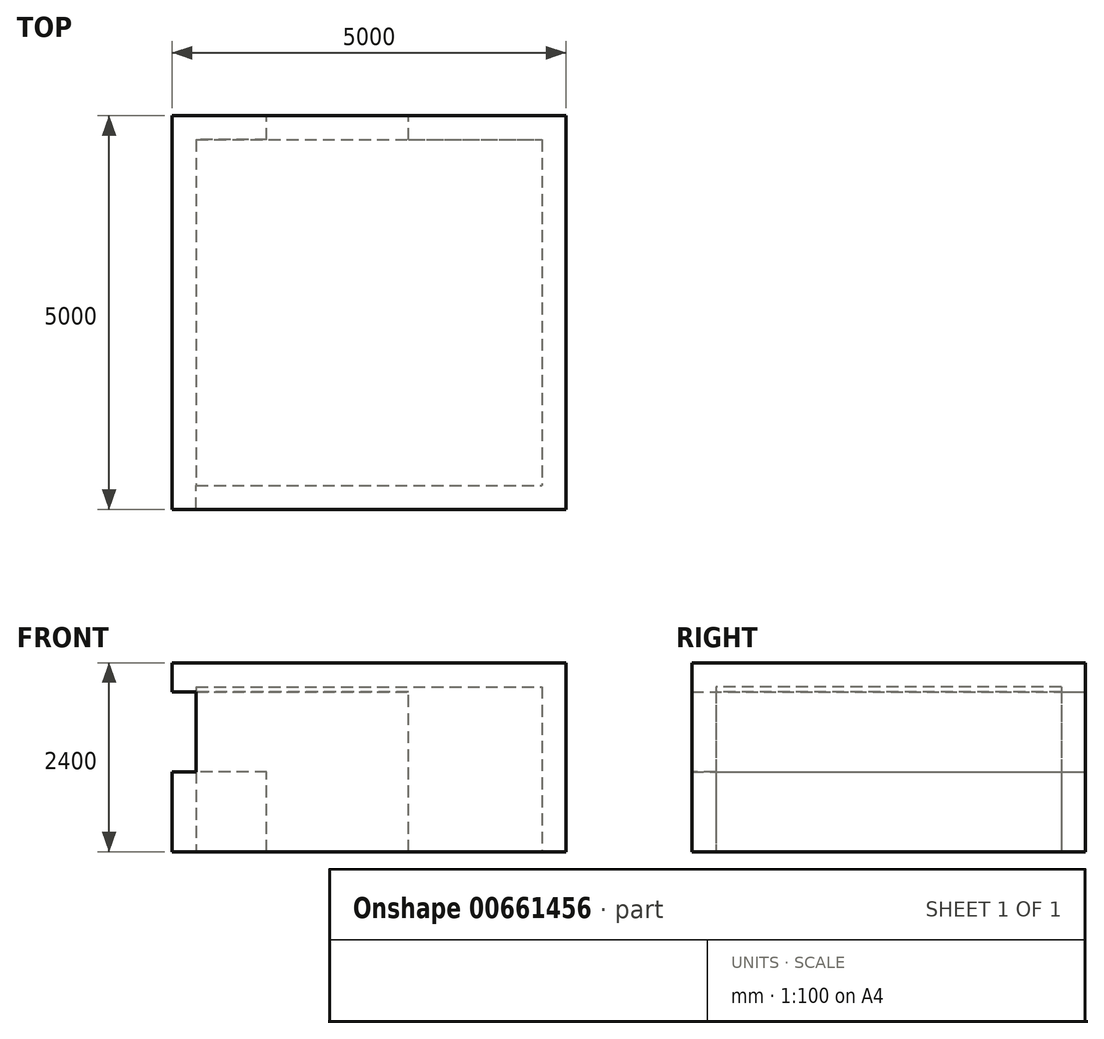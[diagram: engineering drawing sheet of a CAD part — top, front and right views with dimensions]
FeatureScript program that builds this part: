
annotation { "Feature Type Name" : "Feature", "Feature Type Description" : "" }
export const myFeature = defineFeature(function(context is Context, id is Id, definition is map)
    precondition{}
    {
        {
            var Q0;
            Q0=qCreatedBy(makeId("Top.planeOp"),FACE);
            var sketch = newSketch(context, id + "F0", { "sketchPlane" : qUnion([Q0])});
            skLineSegment(sketch, "E0", {"start": v(-2500, 2500) * mm, "end": v(-2500, -2500) * mm});
            skLineSegment(sketch, "E1", {"start": v(-2500, -2500) * mm, "end": v(2500, -2500) * mm});
            skLineSegment(sketch, "E2", {"start": v(2500, 2500) * mm, "end": v(2500, -2500) * mm});
            skLineSegment(sketch, "E3", {"start": v(-2500, 2500) * mm, "end": v(2500, 2500) * mm});
            skSolve(sketch);
        }
        {
            var Q0;
            Q0=makeQuery(id+"F0.imprint","IMPRINT",FACE,{"disambiguationData":[TD([[makeQuery(id+"F0.imprint","IMPRINT",EDGE,{"derivedFrom":sQuery(id+"F0.wireOp",EDGE,"E0")}),1.0]])]});
            extrude(context, id + "F1", {"entities" : qUnion([Q0]), "depth" : 2400 * mm, "offsetDistance" : 25.4 * mm});
        }
        {
            var Q0;
            Q0=makeQuery(id+"F1.opExtrude","CAP_FACE",FACE,{"disambiguationData":[OSD([sQuery(id+"F0.wireOp",EDGE,"E0"),sQuery(id+"F0.wireOp",EDGE,"E1"),sQuery(id+"F0.wireOp",EDGE,"E2"),sQuery(id+"F0.wireOp",EDGE,"E3")])],"isStart":true});
            shell(context, id + "F2", {"entities" : qUnion([Q0]), "thickness" : 304.8 * mm});
        }
        {
            var Q0;
            Q0=makeQuery(id+"F1.opExtrude","SWEPT_FACE",FACE,{"disambiguationData":[OSD([sQuery(id+"F0.wireOp",EDGE,"E3")])]});
            var sketch = newSketch(context, id + "F3", { "sketchPlane" : qUnion([Q0])});
            skLineSegment(sketch, "E4.bottom", {"start": v(-500, 0) * mm, "end": v(1300, 0) * mm});
            skLineSegment(sketch, "E4.top", {"start": v(-500, 2032) * mm, "end": v(1300, 2032) * mm});
            skLineSegment(sketch, "E4.left", {"start": v(-500, 0) * mm, "end": v(-500, 2032) * mm});
            skLineSegment(sketch, "E4.right", {"start": v(1300, 0) * mm, "end": v(1300, 2032) * mm});
            skSolve(sketch);
        }
        {
            var Q0;
            Q0=makeQuery(id+"F3.imprint","IMPRINT",FACE,{"disambiguationData":[TD([[makeQuery(id+"F3.imprint","IMPRINT",EDGE,{"derivedFrom":sQuery(id+"F3.wireOp",EDGE,"E4.bottom")}),-1.0]])]});
            var Q1;
            Q1=makeQuery(id+"F2.opShell","OFFSET_FACE",FACE,{"disambiguationData":[OSD([sQuery(id+"F0.wireOp",EDGE,"E3")])]});
            extrude(context, id + "F4", {"entities" : qUnion([Q0, Q1]), "operationType" : NewBodyOperationType.REMOVE, "oppositeDirection" : true, "depth" : 457.2 * mm, "offsetDistance" : 25.4 * mm});
        }
        {
            var Q0;
            Q0=makeQuery(id+"F1.opExtrude","SWEPT_FACE",FACE,{"disambiguationData":[OSD([sQuery(id+"F0.wireOp",EDGE,"E3")])]});
            var sketch = newSketch(context, id + "F5", { "sketchPlane" : qUnion([Q0])});
            skLineSegment(sketch, "E5", {"start": v(1300, 1016) * mm, "end": v(2500, 1016) * mm});
            skPoint(sketch, "E5.endSnap0", {"position": v(2500, 1200) * mm});
            skLineSegment(sketch, "E6", {"start": v(2500, 1016) * mm, "end": v(2500, 2032) * mm});
            skLineSegment(sketch, "E7", {"start": v(2500, 2032) * mm, "end": v(1300, 2032) * mm});
            skLineSegment(sketch, "E8", {"start": v(1300, 2032) * mm, "end": v(1300, 1016) * mm});
            skSolve(sketch);
        }
        {
            var Q0;
            Q0=makeQuery(id+"F5.imprint","IMPRINT",FACE,{"disambiguationData":[TD([[makeQuery(id+"F5.imprint","IMPRINT",EDGE,{"derivedFrom":sQuery(id+"F5.wireOp",EDGE,"E5")}),1.0]])]});
            extrude(context, id + "F6", {"entities" : qUnion([Q0]), "operationType" : NewBodyOperationType.REMOVE, "oppositeDirection" : true, "depth" : 457.2 * mm, "offsetDistance" : 25.4 * mm});
        }
        {
            var Q0;
            Q0=makeQuery(id+"F1.opExtrude","SWEPT_FACE",FACE,{"disambiguationData":[OSD([sQuery(id+"F0.wireOp",EDGE,"E0")])]});
            var sketch = newSketch(context, id + "F7", { "sketchPlane" : qUnion([Q0])});
            skLineSegment(sketch, "E9", {"start": v(-2042.8, 1016) * mm, "end": v(2500, 1016) * mm});
            skPoint(sketch, "E9.endSnap0", {"position": v(2500, 1200) * mm});
            skLineSegment(sketch, "E10", {"start": v(2500, 1016) * mm, "end": v(2500, 2032) * mm});
            skLineSegment(sketch, "E11", {"start": v(2500, 2032) * mm, "end": v(-2042.8, 2032) * mm});
            skLineSegment(sketch, "E12", {"start": v(-2042.8, 2032) * mm, "end": v(-2042.8, 1016) * mm});
            skSolve(sketch);
        }
        {
            var Q0;
            Q0=makeQuery(id+"F7.imprint","IMPRINT",FACE,{"disambiguationData":[TD([[makeQuery(id+"F7.imprint","IMPRINT",EDGE,{"derivedFrom":sQuery(id+"F7.wireOp",EDGE,"E9")}),1.0]])]});
            extrude(context, id + "F8", {"entities" : qUnion([Q0]), "operationType" : NewBodyOperationType.REMOVE, "oppositeDirection" : true, "depth" : 304.8 * mm, "offsetDistance" : 25.4 * mm});
        }
    });
